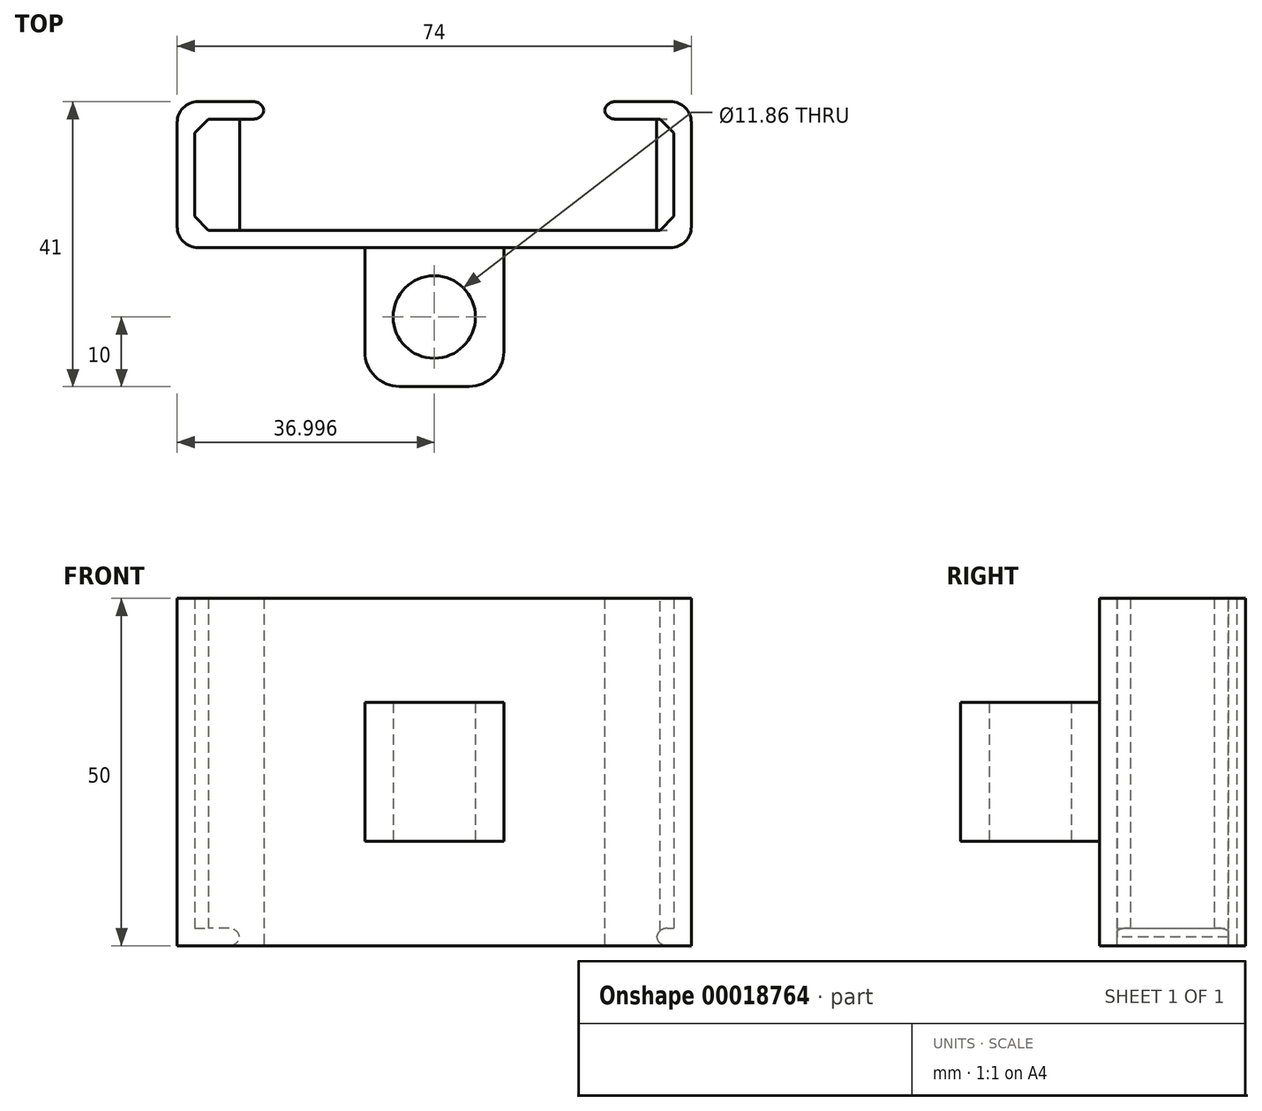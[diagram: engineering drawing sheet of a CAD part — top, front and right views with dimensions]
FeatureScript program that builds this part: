
annotation { "Feature Type Name" : "Feature", "Feature Type Description" : "" }
export const myFeature = defineFeature(function(context is Context, id is Id, definition is map)
    precondition{}
    {
        {
            var Q0;
            Q0=qCreatedBy(makeId("Top.planeOp"),FACE);
            var sketch = newSketch(context, id + "F0", { "sketchPlane" : qUnion([Q0])});
            skLineSegment(sketch, "E0", {"start": v(-24.4, 18.5) * mm, "end": v(-11.9, 18.5) * mm});
            skLineSegment(sketch, "E1", {"start": v(-11.9, 18.5) * mm, "end": v(-11.9, 16) * mm});
            skLineSegment(sketch, "E2", {"start": v(-11.9, 16) * mm, "end": v(-21.9, 16) * mm});
            skLineSegment(sketch, "E3", {"start": v(-21.9, 16) * mm, "end": v(-21.9, 0) * mm});
            skLineSegment(sketch, "E4", {"start": v(-21.9, 0) * mm, "end": v(47.1, 0) * mm});
            skLineSegment(sketch, "E5", {"start": v(47.1, 0) * mm, "end": v(47.1, 16) * mm});
            skLineSegment(sketch, "E6", {"start": v(47.1, 16) * mm, "end": v(37.1, 16) * mm});
            skLineSegment(sketch, "E7", {"start": v(37.1, 16) * mm, "end": v(37.1, 18.5) * mm});
            skLineSegment(sketch, "E8", {"start": v(37.1, 18.5) * mm, "end": v(49.6, 18.5) * mm});
            skLineSegment(sketch, "E9", {"start": v(49.6, 18.5) * mm, "end": v(49.6, -2.5) * mm});
            skLineSegment(sketch, "E10", {"start": v(49.6, -2.5) * mm, "end": v(-24.4, -2.5) * mm});
            skLineSegment(sketch, "E11", {"start": v(-24.4, -2.5) * mm, "end": v(-24.4, 18.5) * mm});
            skLineSegment(sketch, "E12", {"start": v(-15.4, 0) * mm, "end": v(-15.4, 16) * mm});
            skLineSegment(sketch, "E13", {"start": v(44.6, 0) * mm, "end": v(44.6, 16) * mm});
            skSolve(sketch);
        }
        {
            var Q0;
            Q0=makeQuery(id+"F0.imprint","IMPRINT",FACE,{"disambiguationData":[TD([[makeQuery(id+"F0.imprint","IMPRINT",EDGE,{"derivedFrom":sQuery(id+"F0.wireOp",EDGE,"E0")}),-1.0]])]});
            extrude(context, id + "F1", {"entities" : qUnion([Q0]), "depth" : 50 * mm});
        }
        {
            var Q0;
            {var subQ2=sQuery(id+"F0.wireOp",EDGE,"E5");Q0=makeQuery(id+"F0.imprint","IMPRINT",FACE,{"disambiguationData":[TD([[makeQuery(id+"F0.imprint","IMPRINT",EDGE,{"derivedFrom":subQ2}),1.0]])]});}
            var Q1;
            {var subQ2=sQuery(id+"F0.wireOp",EDGE,"E3");Q1=makeQuery(id+"F0.imprint","IMPRINT",FACE,{"disambiguationData":[TD([[makeQuery(id+"F0.imprint","IMPRINT",EDGE,{"derivedFrom":subQ2}),1.0]])]});}
            extrude(context, id + "F2", {"entities" : qUnion([Q0, Q1]), "operationType" : NewBodyOperationType.ADD, "depth" : 2.5 * mm});
        }
        {
            var Q0;
            Q0=makeQuery(id+"F1.opExtrude","SWEPT_EDGE",EDGE,{"disambiguationData":[OSD([sQuery(id+"F0.wireOp",EDGE,"E4"),sQuery(id+"F0.wireOp",EDGE,"E5")])]});
            var Q1;
            Q1=makeQuery(id+"F1.opExtrude","SWEPT_EDGE",EDGE,{"disambiguationData":[OSD([sQuery(id+"F0.wireOp",EDGE,"E5"),sQuery(id+"F0.wireOp",EDGE,"E6")])]});
            var Q2;
            Q2=makeQuery(id+"F1.opExtrude","SWEPT_EDGE",EDGE,{"disambiguationData":[OSD([sQuery(id+"F0.wireOp",EDGE,"E3"),sQuery(id+"F0.wireOp",EDGE,"E4")])]});
            var Q3;
            Q3=makeQuery(id+"F1.opExtrude","SWEPT_EDGE",EDGE,{"disambiguationData":[OSD([sQuery(id+"F0.wireOp",EDGE,"E2"),sQuery(id+"F0.wireOp",EDGE,"E3")])]});
            chamfer(context, id + "F3", {"entities" : qUnion([Q0, Q1, Q2, Q3]), "width" : 2 * mm, "tangentPropagation" : true});
        }
        {
            var Q0;
            Q0=makeQuery(id+"F1.opExtrude","SWEPT_EDGE",EDGE,{"disambiguationData":[OSD([sQuery(id+"F0.wireOp",EDGE,"E0"),sQuery(id+"F0.wireOp",EDGE,"E11")])]});
            var Q1;
            Q1=makeQuery(id+"F1.opExtrude","SWEPT_EDGE",EDGE,{"disambiguationData":[OSD([sQuery(id+"F0.wireOp",EDGE,"E10"),sQuery(id+"F0.wireOp",EDGE,"E11")])]});
            var Q2;
            Q2=makeQuery(id+"F1.opExtrude","SWEPT_EDGE",EDGE,{"disambiguationData":[OSD([sQuery(id+"F0.wireOp",EDGE,"E9"),sQuery(id+"F0.wireOp",EDGE,"E10")])]});
            var Q3;
            Q3=makeQuery(id+"F1.opExtrude","SWEPT_EDGE",EDGE,{"disambiguationData":[OSD([sQuery(id+"F0.wireOp",EDGE,"E8"),sQuery(id+"F0.wireOp",EDGE,"E9")])]});
            fillet(context, id + "F4", {"entities" : qUnion([Q0, Q1, Q2, Q3]), "radius" : 3 * mm, "tangentPropagation" : true, "allowEdgeOverflow" : false});
        }
        {
            var Q0;
            Q0=makeQuery(id+"F1.opExtrude","SWEPT_EDGE",EDGE,{"disambiguationData":[OSD([sQuery(id+"F0.wireOp",EDGE,"E1"),sQuery(id+"F0.wireOp",EDGE,"E2")])]});
            var Q1;
            Q1=makeQuery(id+"F1.opExtrude","SWEPT_EDGE",EDGE,{"disambiguationData":[OSD([sQuery(id+"F0.wireOp",EDGE,"E0"),sQuery(id+"F0.wireOp",EDGE,"E1")])]});
            var Q2;
            Q2=makeQuery(id+"F1.opExtrude","SWEPT_EDGE",EDGE,{"disambiguationData":[OSD([sQuery(id+"F0.wireOp",EDGE,"E7"),sQuery(id+"F0.wireOp",EDGE,"E8")])]});
            var Q3;
            Q3=makeQuery(id+"F1.opExtrude","SWEPT_EDGE",EDGE,{"disambiguationData":[OSD([sQuery(id+"F0.wireOp",EDGE,"E6"),sQuery(id+"F0.wireOp",EDGE,"E7")])]});
            var Q4;
            Q4=makeQuery(id+"F2.opExtrude","CAP_EDGE",EDGE,{"disambiguationData":[OSD([sQuery(id+"F0.wireOp",EDGE,"E13")])],"isStart":false});
            var Q5;
            Q5=makeQuery(id+"F2.opExtrude","CAP_EDGE",EDGE,{"disambiguationData":[OSD([sQuery(id+"F0.wireOp",EDGE,"E13")])],"isStart":true});
            var Q6;
            Q6=makeQuery(id+"F2.opExtrude","CAP_EDGE",EDGE,{"disambiguationData":[OSD([sQuery(id+"F0.wireOp",EDGE,"E12")])],"isStart":false});
            var Q7;
            Q7=makeQuery(id+"F2.opExtrude","CAP_EDGE",EDGE,{"disambiguationData":[OSD([sQuery(id+"F0.wireOp",EDGE,"E12")])],"isStart":true});
            fillet(context, id + "F5", {"entities" : qUnion([Q0, Q1, Q2, Q3, Q4, Q5, Q6, Q7]), "radius" : 1.5 * mm, "tangentPropagation" : true, "allowEdgeOverflow" : false});
        }
        {
            var Q0;
            Q0=makeQuery(id+"F1.opExtrude","SWEPT_FACE",FACE,{"disambiguationData":[OSD([sQuery(id+"F0.wireOp",EDGE,"E10")])]});
            var sketch = newSketch(context, id + "F6", { "sketchPlane" : qUnion([Q0])});
            skLineSegment(sketch, "E14.bottom", {"start": v(22.6, 35) * mm, "end": v(2.6, 35) * mm});
            skLineSegment(sketch, "E14.top", {"start": v(22.6, 15) * mm, "end": v(2.6, 15) * mm});
            skLineSegment(sketch, "E14.left", {"start": v(22.6, 35) * mm, "end": v(22.6, 15) * mm});
            skLineSegment(sketch, "E14.right", {"start": v(2.6, 35) * mm, "end": v(2.6, 15) * mm});
            skSolve(sketch);
        }
        {
            var Q0;
            Q0=qSketchRegion(id+"F6",true);
            extrude(context, id + "F7", {"entities" : qUnion([Q0]), "operationType" : NewBodyOperationType.ADD, "depth" : 20 * mm});
        }
        {
            var Q0;
            Q0=makeQuery(id+"F7.opExtrude","SWEPT_FACE",FACE,{"disambiguationData":[OSD([sQuery(id+"F6.wireOp",EDGE,"E14.top")])]});
            var sketch = newSketch(context, id + "F8", { "sketchPlane" : qUnion([Q0])});
            skCircle(sketch, "E15", {"center": v(12.6, 12.5) * mm, "radius": 5.93 * mm});
            skSolve(sketch);
        }
        {
            var Q0;
            Q0=qSketchRegion(id+"F8",true);
            extrude(context, id + "F9", {"entities" : qUnion([Q0]), "operationType" : NewBodyOperationType.REMOVE, "oppositeDirection" : true, "depth" : 25 * mm});
        }
        {
            var Q0;
            Q0=makeQuery(id+"F7.opExtrude","CAP_EDGE",EDGE,{"disambiguationData":[OSD([sQuery(id+"F6.wireOp",EDGE,"E14.right")])],"isStart":true});
            var Q1;
            Q1=makeQuery(id+"F7.opExtrude","CAP_EDGE",EDGE,{"disambiguationData":[OSD([sQuery(id+"F6.wireOp",EDGE,"E14.right")])],"isStart":false});
            var Q2;
            Q2=makeQuery(id+"F7.opExtrude","CAP_EDGE",EDGE,{"disambiguationData":[OSD([sQuery(id+"F6.wireOp",EDGE,"E14.left")])],"isStart":false});
            var Q3;
            Q3=makeQuery(id+"F7.opExtrude","CAP_EDGE",EDGE,{"disambiguationData":[OSD([sQuery(id+"F6.wireOp",EDGE,"E14.left")])],"isStart":true});
            var Q4;
            Q4=makeQuery(id+"F7.opExtrude","CAP_EDGE",EDGE,{"disambiguationData":[OSD([sQuery(id+"F6.wireOp",EDGE,"E14.top")])],"isStart":true});
            var Q5;
            Q5=makeQuery(id+"F7.opExtrude","CAP_EDGE",EDGE,{"disambiguationData":[OSD([sQuery(id+"F6.wireOp",EDGE,"E14.bottom")])],"isStart":true});
            fillet(context, id + "F10", {"entities" : qUnion([Q0, Q1, Q2, Q3, Q4, Q5]), "radius" : 5 * mm, "tangentPropagation" : true, "allowEdgeOverflow" : false});
        }
    });
